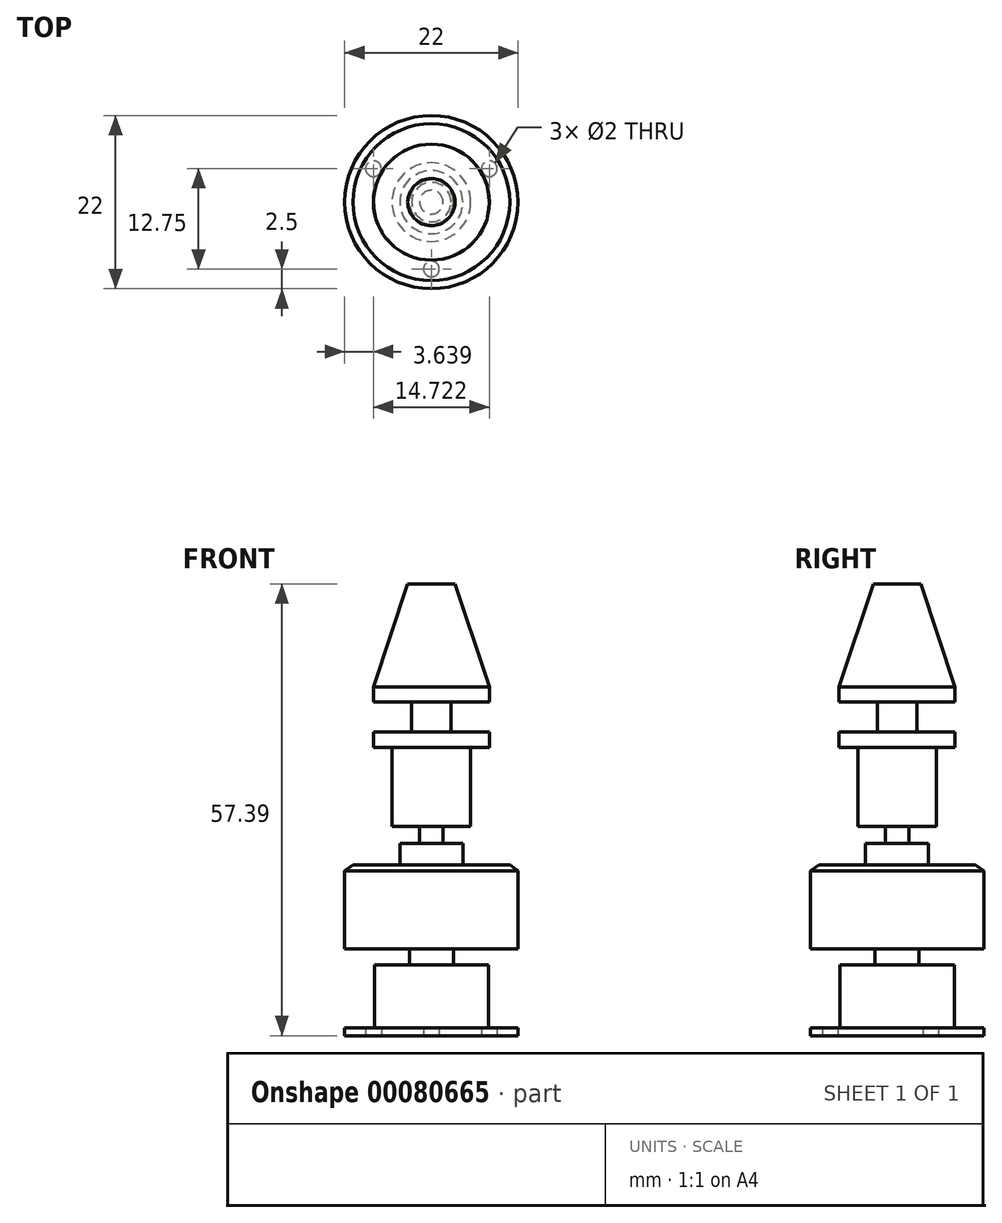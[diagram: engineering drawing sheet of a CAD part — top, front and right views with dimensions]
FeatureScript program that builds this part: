
annotation { "Feature Type Name" : "Feature", "Feature Type Description" : "" }
export const myFeature = defineFeature(function(context is Context, id is Id, definition is map)
    precondition{}
    {
        {
            var Q0;
            Q0=qCreatedBy(makeId("Right.planeOp"),FACE);
            var sketch = newSketch(context, id + "F0", { "sketchPlane" : qUnion([Q0])});
            skLineSegment(sketch, "E0.top", {"start": v(3, 36.45) * mm, "end": v(0, 36.45) * mm});
            skPoint(sketch, "E0.middle", {"position": v(0, 27.26) * mm});
            skLineSegment(sketch, "E1.MirrorCS", {"start": v(7.37, 23.35) * mm, "end": v(3, 36.45) * mm});
            skLineSegment(sketch, "E2.bottom", {"start": v(7.37, 15.65) * mm, "end": v(0, 15.65) * mm});
            skLineSegment(sketch, "E2.top", {"start": v(7.37, 17.65) * mm, "end": v(0, 17.65) * mm});
            skLineSegment(sketch, "E2.left", {"start": v(7.37, 15.65) * mm, "end": v(7.37, 17.65) * mm});
            skPoint(sketch, "E2.middle", {"position": v(0, 16.65) * mm});
            skLineSegment(sketch, "E3", {"start": v(0, 23.35) * mm, "end": v(7.37, 23.35) * mm});
            skLineSegment(sketch, "E4", {"start": v(7.37, 23.35) * mm, "end": v(7.37, 21.45) * mm});
            skLineSegment(sketch, "E5", {"start": v(7.37, 21.45) * mm, "end": v(0, 21.45) * mm});
            skLineSegment(sketch, "E6.MirrorCS", {"start": v(2.5, 21.45) * mm, "end": v(2.5, 17.65) * mm});
            skLineSegment(sketch, "E7.bottom", {"start": v(0, 15.65) * mm, "end": v(5, 15.65) * mm});
            skLineSegment(sketch, "E7.top", {"start": v(0, 5.65) * mm, "end": v(5, 5.65) * mm});
            skLineSegment(sketch, "E7.right", {"start": v(5, 15.65) * mm, "end": v(5, 5.65) * mm});
            skLineSegment(sketch, "E8", {"start": v(0, 5.65) * mm, "end": v(1.5, 5.65) * mm});
            skLineSegment(sketch, "E9.bottom", {"start": v(4, 0.77) * mm, "end": v(0, 0.77) * mm});
            skLineSegment(sketch, "E9.top", {"start": v(4, 3.45) * mm, "end": v(0, 3.45) * mm});
            skLineSegment(sketch, "E9.left", {"start": v(4, 0.77) * mm, "end": v(4, 3.45) * mm});
            skPoint(sketch, "E9.middle", {"position": v(0, 2.11) * mm});
            skLineSegment(sketch, "E10.MirrorCS", {"start": v(1.5, 5.65) * mm, "end": v(1.5, 3.45) * mm});
            skLineSegment(sketch, "E11.MirrorCS", {"start": v(11, 0) * mm, "end": v(9.96, 0.77) * mm});
            skLineSegment(sketch, "E12", {"start": v(11, 0) * mm, "end": v(11, -9.94) * mm});
            skLineSegment(sketch, "E13", {"start": v(0, 51.02) * mm, "end": v(0, -49.34) * mm, "construction": true});
            skLineSegment(sketch, "E14.MirrorCS", {"start": v(0, -11.94) * mm, "end": v(7.25, -11.94) * mm});
            skLineSegment(sketch, "E15.MirrorCS", {"start": v(7.25, -11.94) * mm, "end": v(7.25, -19.94) * mm});
            skLineSegment(sketch, "E16.MirrorCS", {"start": v(7.25, -19.94) * mm, "end": v(0, -19.94) * mm});
            skLineSegment(sketch, "E17.MirrorCS", {"start": v(2.8, -9.94) * mm, "end": v(2.8, -11.94) * mm});
            skLineSegment(sketch, "E18.bottom", {"start": v(0, -19.94) * mm, "end": v(11, -19.94) * mm});
            skLineSegment(sketch, "E18.top", {"start": v(0, -20.94) * mm, "end": v(11, -20.94) * mm});
            skLineSegment(sketch, "E18.right", {"start": v(11, -19.94) * mm, "end": v(11, -20.94) * mm});
            skPoint(sketch, "E19.end.orphan", {"position": v(-3, 36.45) * mm});
            skPoint(sketch, "E20.end.orphan", {"position": v(-2.5, 17.65) * mm});
            skPoint(sketch, "E21.trimOffspring.start.orphan", {"position": v(-2.5, 21.45) * mm});
            skPoint(sketch, "E22.end.orphan", {"position": v(-7.37, 23.35) * mm});
            skPoint(sketch, "E22.start.orphan", {"position": v(-7.37, 21.45) * mm});
            skPoint(sketch, "E2.right.end.orphan", {"position": v(-7.37, 17.65) * mm});
            skPoint(sketch, "E2.right.start.orphan", {"position": v(-7.37, 15.65) * mm});
            skPoint(sketch, "E23.end.orphan", {"position": v(-1.5, 3.45) * mm});
            skPoint(sketch, "E9.right.end.orphan", {"position": v(-4, 3.45) * mm});
            skLineSegment(sketch, "E24.trimOffspring", {"start": v(0, 0.77) * mm, "end": v(9.96, 0.77) * mm});
            skPoint(sketch, "E25.end.orphan", {"position": v(-9.96, 0.77) * mm});
            skPoint(sketch, "E26.left.start.orphan", {"position": v(-11, 0) * mm});
            skPoint(sketch, "E27.orphan", {"position": v(-4, 0.77) * mm});
            skLineSegment(sketch, "E28.trimOffspring", {"start": v(0, -9.94) * mm, "end": v(11, -9.94) * mm});
            skPoint(sketch, "E26.top.start.orphan", {"position": v(-11, -9.94) * mm});
            skPoint(sketch, "E29.end.orphan", {"position": v(-2.8, -11.94) * mm});
            skPoint(sketch, "E29.start.orphan", {"position": v(-2.8, -9.94) * mm});
            skPoint(sketch, "E30.orphan", {"position": v(0, -11.94) * mm});
            skPoint(sketch, "E31.MirrorCS.end.orphan", {"position": v(-7.25, -11.94) * mm});
            skPoint(sketch, "E32.end.orphan", {"position": v(0, -19.94) * mm});
            skPoint(sketch, "E32.start.orphan", {"position": v(-7.25, -19.94) * mm});
            skPoint(sketch, "E18.left.start.orphan", {"position": v(-11, -19.94) * mm});
            skLineSegment(sketch, "E33", {"start": v(0, 36.45) * mm, "end": v(0, -20.94) * mm});
            skPoint(sketch, "E34.orphan", {"position": v(-1.5, 5.65) * mm});
            skSolve(sketch);
        }
        {
            var Q0;
            Q0 = qSketchRegion(id + "F0", true);
            var Q1;
            Q1=sQuery(id+"F0.wireOp",EDGE,"E33");
            revolve(context, id + "F1", {"entities" : qUnion([Q0]), "axis" : qUnion([Q1]), "revolveType" : RevolveType.FULL});
        }
        {
            var Q0;
            Q0=makeQuery(id+"F1.opRevolve","SWEPT_FACE",FACE,{"disambiguationData":[OSD([sQuery(id+"F0.wireOp",EDGE,"E18.top")])]});
            var sketch = newSketch(context, id + "F2", { "sketchPlane" : qUnion([Q0])});
            skCircle(sketch, "E35", {"center": v(0, 8.5) * mm, "radius": 1 * mm});
            skCircle(sketch, "E36.1.0", {"center": v(-7.36, -4.25) * mm, "radius": 1 * mm});
            skCircle(sketch, "E36.2.0", {"center": v(7.36, -4.25) * mm, "radius": 1 * mm});
            skPoint(sketch, "E36.center", {"position": v(0, 0) * mm});
            skSolve(sketch);
        }
        {
            var Q0;
            Q0 = qSketchRegion(id + "F2", true);
            extrude(context, id + "F3", {"entities" : qUnion([Q0]), "operationType" : NewBodyOperationType.REMOVE, "oppositeDirection" : true, "depth" : 2 * mm});
        }
    });
